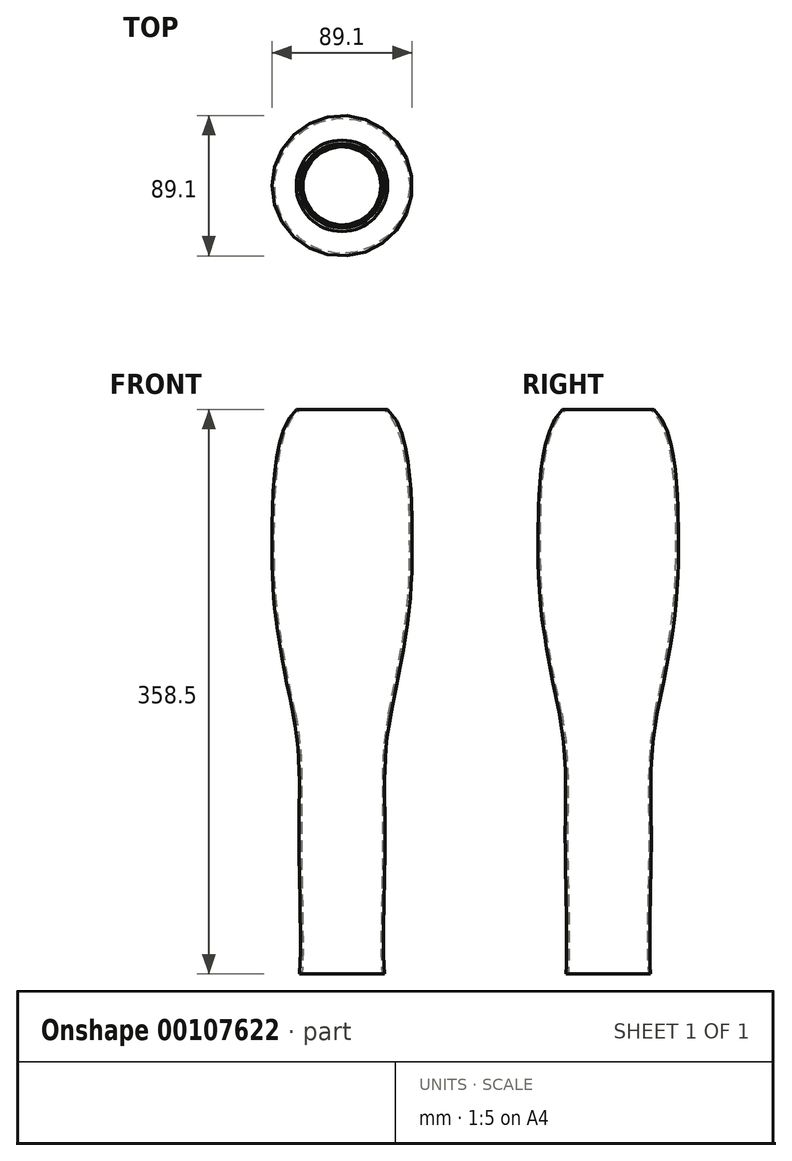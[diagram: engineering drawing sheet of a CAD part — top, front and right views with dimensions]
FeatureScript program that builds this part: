
annotation { "Feature Type Name" : "Feature", "Feature Type Description" : "" }
export const myFeature = defineFeature(function(context is Context, id is Id, definition is map)
    precondition{}
    {
        {
            var Q0;
            Q0=qCreatedBy(makeId("Front.planeOp"),FACE);
            var sketch = newSketch(context, id + "F0", { "sketchPlane" : qUnion([Q0])});
            skLineSegment(sketch, "E0", {"start": v(29, 128) * mm, "end": v(0, 128) * mm, "construction": true});
            skLineSegment(sketch, "E1", {"start": v(0, 128) * mm, "end": v(0, -65.5) * mm, "construction": true});
            skLineSegment(sketch, "E2", {"start": v(0, -65.5) * mm, "end": v(31, -65.5) * mm, "construction": true});
            skLineSegment(sketch, "E3", {"start": v(29, 128) * mm, "end": v(0, 128) * mm});
            skLineSegment(sketch, "E4", {"start": v(0, -65.5) * mm, "end": v(31, -65.5) * mm});
            skLineSegment(sketch, "E5", {"start": v(0, -65.5) * mm, "end": v(0, 128) * mm});
            skFitSpline(sketch, "E6", {"points": [v(31, -65.5) * mm, v(42.57, 0) * mm, v(44.5, 50.52) * mm, v(29, 128) * mm], "startDerivative": vector(51.23, 239.67) * mm, "endDerivative": vector(-115.1, 100.3) * mm});
            skLineSegment(sketch, "E7", {"start": v(0, 128) * mm, "end": v(0, 0) * mm, "construction": true});
            skLineSegment(sketch, "E8", {"start": v(0, 0) * mm, "end": v(0, -65.5) * mm, "construction": true});
            skSolve(sketch);
        }
        {
            var Q0;
            Q0=makeQuery(id+"F0.imprint","IMPRINT",FACE,{"disambiguationData":[TD([[makeQuery(id+"F0.imprint","IMPRINT",EDGE,{"derivedFrom":sQuery(id+"F0.wireOp",EDGE,"E3")}),1.0]])]});
            var Q1;
            Q1=sQuery(id+"F0.wireOp",EDGE,"E5");
            revolve(context, id + "F1", {"entities" : qUnion([Q0]), "axis" : qUnion([Q1]), "revolveType" : RevolveType.FULL});
        }
        {
            var Q0;
            Q0=makeQuery(id+"F1.opRevolve","SWEPT_FACE",FACE,{"disambiguationData":[OSD([sQuery(id+"F0.wireOp",EDGE,"E4")])]});
            cPlane(context, id + "F2", {"entities" : qUnion([Q0]), "cplaneType" : CPlaneType.OFFSET, "offset" : 165 * mm, "width" : 150 * mm, "height" : 150 * mm});
        }
        {
            var Q0;
            Q0=qCreatedBy(id+"F2.planeOp",FACE);
            var sketch = newSketch(context, id + "F3", { "sketchPlane" : qUnion([Q0])});
            skPoint(sketch, "E9", {"position": v(0, 0) * mm});
            skSolve(sketch);
        }
        {
            var Q0;
            Q0=qCreatedBy(makeId("Front.planeOp"),FACE);
            var sketch = newSketch(context, id + "F4", { "sketchPlane" : qUnion([Q0])});
            skLineSegment(sketch, "E10.0", {"start": v(31, -65.5) * mm, "end": v(-31, -65.5) * mm, "construction": true});
            skPoint(sketch, "E11.0", {"position": v(0, -230.5) * mm});
            skLineSegment(sketch, "E12", {"start": v(31, -65.5) * mm, "end": v(0, -65.5) * mm});
            skLineSegment(sketch, "E13", {"start": v(0, -65.5) * mm, "end": v(0, -230.5) * mm});
            skLineSegment(sketch, "E14", {"start": v(0, -230.5) * mm, "end": v(26.9, -230.5) * mm});
            skPoint(sketch, "E15.end.orphan", {"position": v(46.65, -230.5) * mm});
            skFitSpline(sketch, "E16", {"points": [v(31, -65.5) * mm, v(27.34, -143.25) * mm, v(26.9, -230.5) * mm], "startDerivative": vector(-33.03, -173.94) * mm, "endDerivative": vector(8.23, -122.17) * mm});
            skSolve(sketch);
        }
        {
            var Q0;
            Q0=makeQuery(id+"F4.imprint","IMPRINT",FACE,{"disambiguationData":[TD([[makeQuery(id+"F4.imprint","IMPRINT",EDGE,{"derivedFrom":sQuery(id+"F4.wireOp",EDGE,"E12")}),1.0]])]});
            var Q1;
            Q1=sQuery(id+"F4.wireOp",EDGE,"E13");
            revolve(context, id + "F5", {"operationType" : NewBodyOperationType.ADD, "entities" : qUnion([Q0]), "axis" : qUnion([Q1]), "revolveType" : RevolveType.FULL});
        }
        {
            var Q0;
            Q0=makeQuery(id+"F5.boolean.opBoolean","MERGE",EDGE,{"derivedFrom":[makeQuery(id+"F1.opRevolve","SWEPT_EDGE",EDGE,{"disambiguationData":[OSD([sQuery(id+"F0.wireOp",EDGE,"E4"),sQuery(id+"F0.wireOp",EDGE,"307aaf62-0fb3-464b-95eb-5698d7bd1ca0")])]}),makeQuery(id+"F5.opRevolve","SWEPT_EDGE",EDGE,{"disambiguationData":[OSD([sQuery(id+"F4.wireOp",EDGE,"E12"),sQuery(id+"F4.wireOp",EDGE,"6d901fea-081b-41e2-b857-a2a5e25bd2c2")])]})]});
            fillet(context, id + "F6", {"entities" : qUnion([Q0]), "radius" : 10 * mm, "tangentPropagation" : true, "allowEdgeOverflow" : false});
        }
        {
            var Q0;
            Q0=makeQuery(id+"F5.opRevolve","SWEPT_FACE",FACE,{"disambiguationData":[OSD([sQuery(id+"F4.wireOp",EDGE,"E14")])]});
            var Q1;
            Q1=makeQuery(id+"F1.opRevolve","SWEPT_FACE",FACE,{"disambiguationData":[OSD([sQuery(id+"F0.wireOp",EDGE,"E3")])]});
            shell(context, id + "F7", {"entities" : qUnion([Q0, Q1]), "thickness" : 1.5 * mm});
        }
    });
